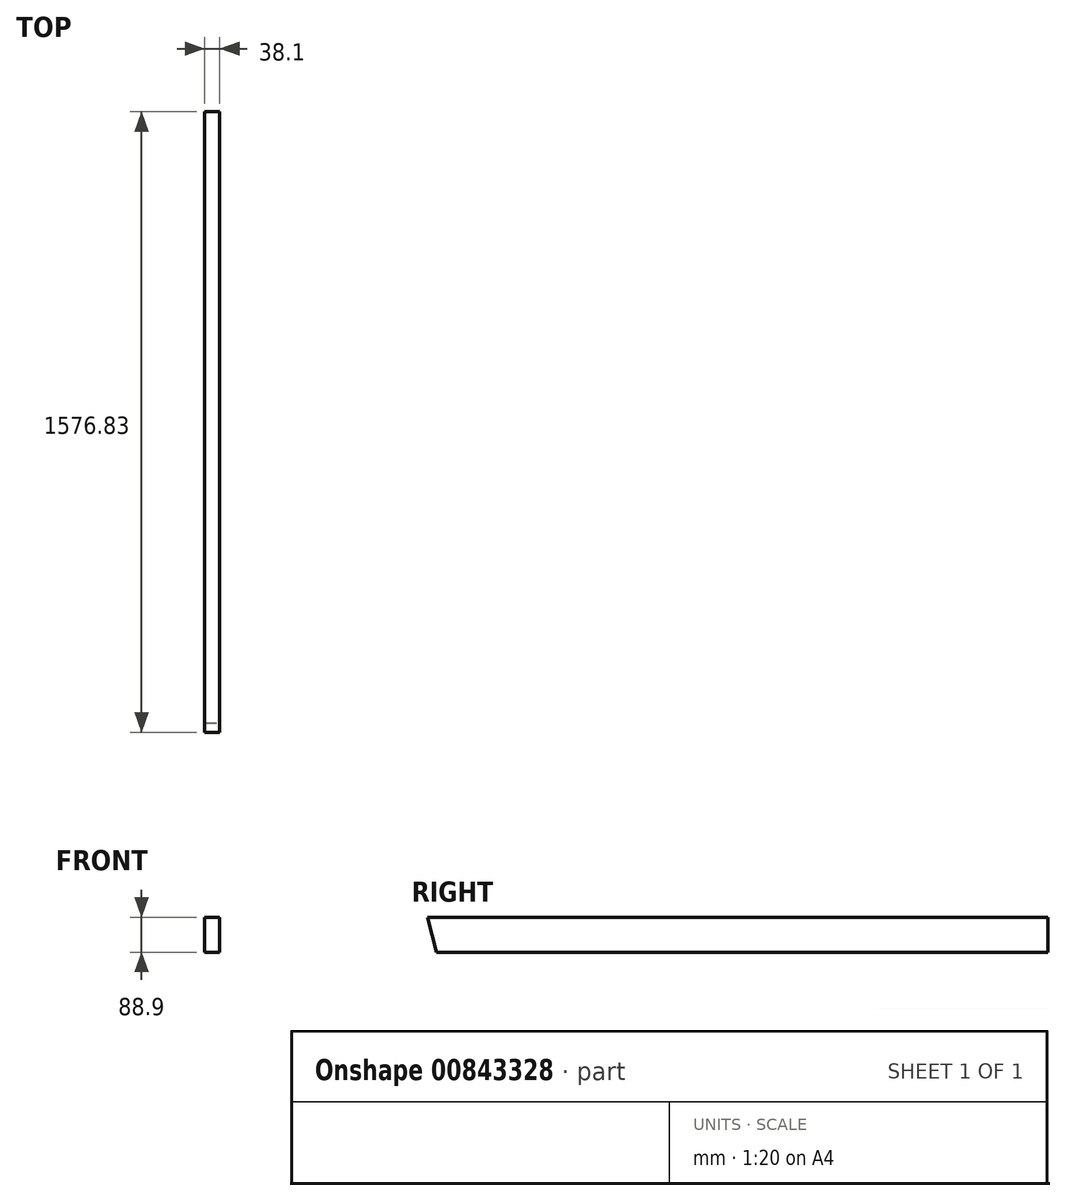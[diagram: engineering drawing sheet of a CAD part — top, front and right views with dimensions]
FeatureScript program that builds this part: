
annotation { "Feature Type Name" : "Feature", "Feature Type Description" : "" }
export const myFeature = defineFeature(function(context is Context, id is Id, definition is map)
    precondition{}
    {
        {
            var Q0;
            Q0=qCreatedBy(makeId("Front.planeOp"),FACE);
            var sketch = newSketch(context, id + "F0", { "sketchPlane" : qUnion([Q0])});
            skLineSegment(sketch, "E0.bottom", {"start": v(19.05, -44.45) * mm, "end": v(-19.05, -44.45) * mm});
            skLineSegment(sketch, "E0.top", {"start": v(19.05, 44.45) * mm, "end": v(-19.05, 44.45) * mm});
            skLineSegment(sketch, "E0.left", {"start": v(19.05, -44.45) * mm, "end": v(19.05, 44.45) * mm});
            skLineSegment(sketch, "E0.right", {"start": v(-19.05, -44.45) * mm, "end": v(-19.05, 44.45) * mm});
            skPoint(sketch, "E0.middle", {"position": v(0, 0) * mm});
            skSolve(sketch);
        }
        {
            var Q0;
            Q0=makeQuery(id+"F0.imprint","IMPRINT",FACE,{"disambiguationData":[TD([[makeQuery(id+"F0.imprint","IMPRINT",EDGE,{"derivedFrom":sQuery(id+"F0.wireOp",EDGE,"E0.bottom")}),-1.0]])]});
            extrude(context, id + "F1", {"entities" : qUnion([Q0]), "depth" : 1576.83 * mm, "offsetDistance" : 25.4 * mm});
        }
        {
            var Q0;
            Q0=qCreatedBy(makeId("Right.planeOp"),FACE);
            var sketch = newSketch(context, id + "F2", { "sketchPlane" : qUnion([Q0])});
            skLineSegment(sketch, "E1", {"start": v(-1576.83, 44.45) * mm, "end": v(-1552.96, -44.45) * mm});
            skLineSegment(sketch, "E2", {"start": v(-1552.96, -44.45) * mm, "end": v(-1576.83, -44.45) * mm});
            skLineSegment(sketch, "E3", {"start": v(-1576.83, -44.45) * mm, "end": v(-1576.83, 44.45) * mm});
            skSolve(sketch);
        }
        {
            var Q0;
            Q0 = qSketchRegion(id + "F2", true);
            extrude(context, id + "F3", {"entities" : qUnion([Q0]), "operationType" : NewBodyOperationType.REMOVE, "oppositeDirection" : true, "depth" : 50.8 * mm, "offsetDistance" : 25.4 * mm, "symmetric" : true});
        }
    });
